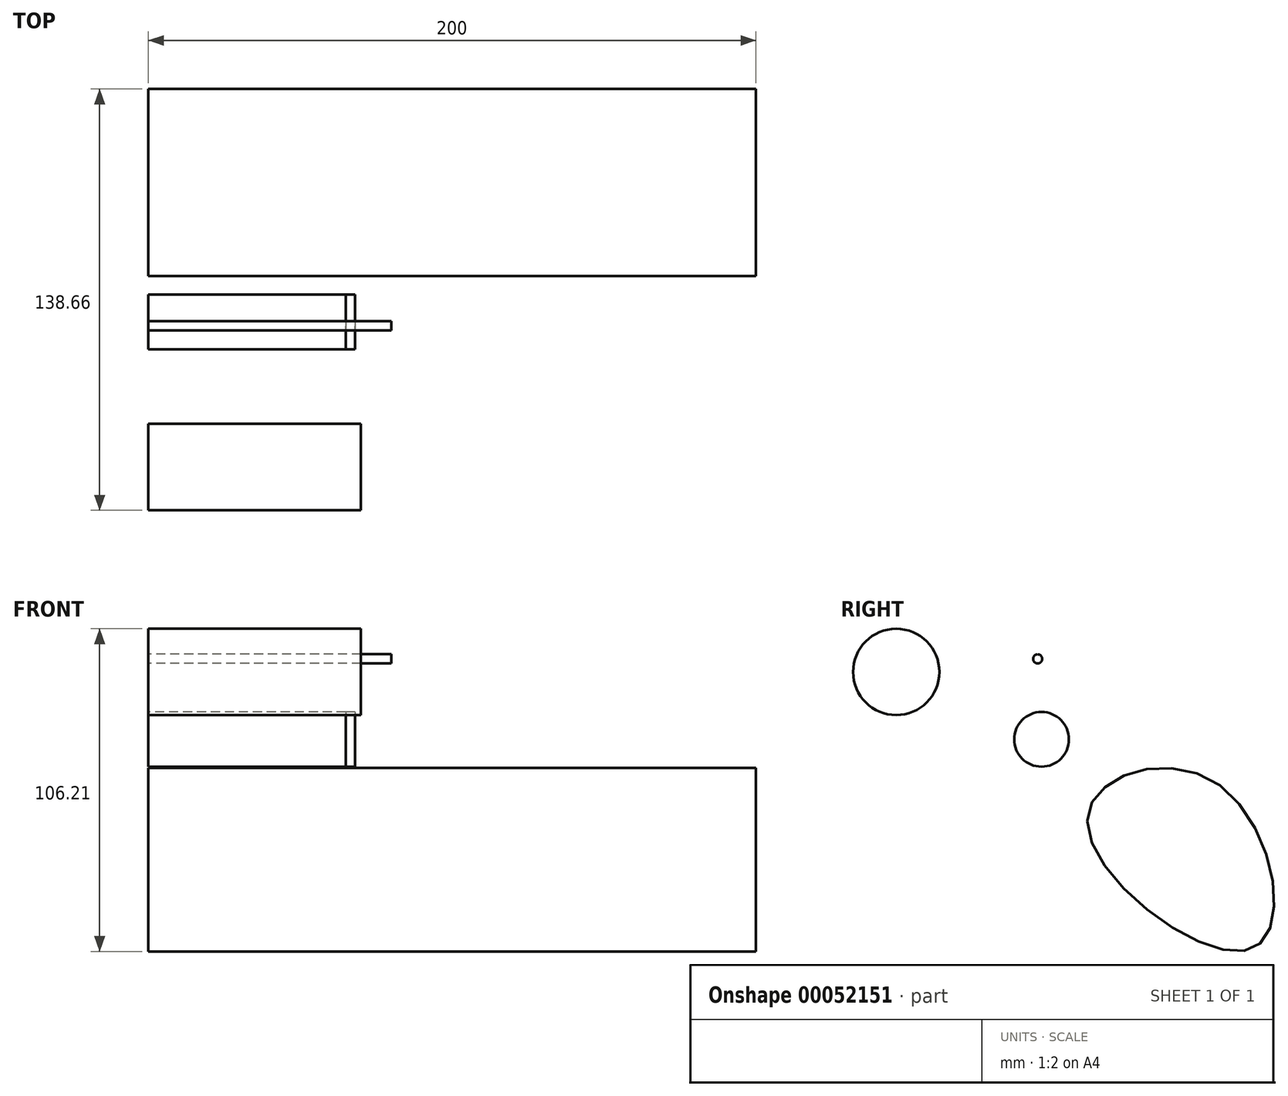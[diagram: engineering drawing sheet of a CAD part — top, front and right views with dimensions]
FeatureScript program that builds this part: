
annotation { "Feature Type Name" : "Feature", "Feature Type Description" : "" }
export const myFeature = defineFeature(function(context is Context, id is Id, definition is map)
    precondition{}
    {
        {
            var Q0;
            Q0=qCreatedBy(makeId("Right.planeOp"),FACE);
            var sketch = newSketch(context, id + "F0", { "sketchPlane" : qUnion([Q0])});
            skCircle(sketch, "E0", {"center": v(-14, 7.22) * mm, "radius": 9 * mm});
            skSolve(sketch);
        }
        {
            var Q0;
            Q0=makeQuery(id+"F0.imprint","IMPRINT",FACE,{"disambiguationData":[TD([[makeQuery(id+"F0.imprint","IMPRINT",EDGE,{"derivedFrom":sQuery(id+"F0.wireOp",EDGE,"E0")}),1.0]])]});
            extrude(context, id + "F1", {"entities" : qUnion([Q0]), "depth" : 65 * mm});
        }
        {
            var Q0;
            Q0=qCreatedBy(makeId("Right.planeOp"),FACE);
            var sketch = newSketch(context, id + "F2", { "sketchPlane" : qUnion([Q0])});
            skCircle(sketch, "E1", {"center": v(-15.3, 33.72) * mm, "radius": 1.5 * mm});
            skSolve(sketch);
        }
        {
            var Q0;
            Q0=qCreatedBy(makeId("Right.planeOp"),FACE);
            var sketch = newSketch(context, id + "F3", { "sketchPlane" : qUnion([Q0])});
            skCircle(sketch, "E2", {"center": v(-61.84, 29.41) * mm, "radius": 14.2 * mm});
            skSolve(sketch);
        }
        {
            var Q0;
            Q0=makeQuery(id+"F2.imprint","IMPRINT",FACE,{"disambiguationData":[TD([[makeQuery(id+"F2.imprint","IMPRINT",EDGE,{"derivedFrom":sQuery(id+"F2.wireOp",EDGE,"E1")}),1.0]])]});
            extrude(context, id + "F4", {"entities" : qUnion([Q0]), "depth" : 80 * mm});
        }
        {
            var Q0;
            Q0=makeQuery(id+"F3.imprint","IMPRINT",FACE,{"disambiguationData":[TD([[makeQuery(id+"F3.imprint","IMPRINT",EDGE,{"derivedFrom":sQuery(id+"F3.wireOp",EDGE,"E2")}),1.0]])]});
            extrude(context, id + "F5", {"entities" : qUnion([Q0]), "depth" : 70 * mm});
        }
        {
            var Q0;
            Q0=makeQuery(id+"F1.opExtrude","CAP_FACE",FACE,{"disambiguationData":[OSD([sQuery(id+"F0.wireOp",EDGE,"E0")])],"isStart":false});
            extrude(context, id + "F6", {"entities" : qUnion([Q0]), "depth" : 3 * mm});
        }
        {
            var Q0;
            Q0=qCreatedBy(makeId("Right.planeOp"),FACE);
            var sketch = newSketch(context, id + "F7", { "sketchPlane" : qUnion([Q0])});
            skFitSpline(sketch, "E3", {"points": [v(1.05, -19.75) * mm, v(43.43, -7.06) * mm, v(55.69, -61.56) * mm, v(1.05, -19.75) * mm]});
            skSolve(sketch);
        }
        {
            var Q0;
            Q0=makeQuery(id+"F7.imprint","IMPRINT",FACE,{"disambiguationData":[TD([[makeQuery(id+"F7.imprint","IMPRINT",EDGE,{"derivedFrom":sQuery(id+"F7.wireOp",EDGE,"E3")}),-1.0]])]});
            extrude(context, id + "F8", {"entities" : qUnion([Q0]), "depth" : 200 * mm});
        }
    });
